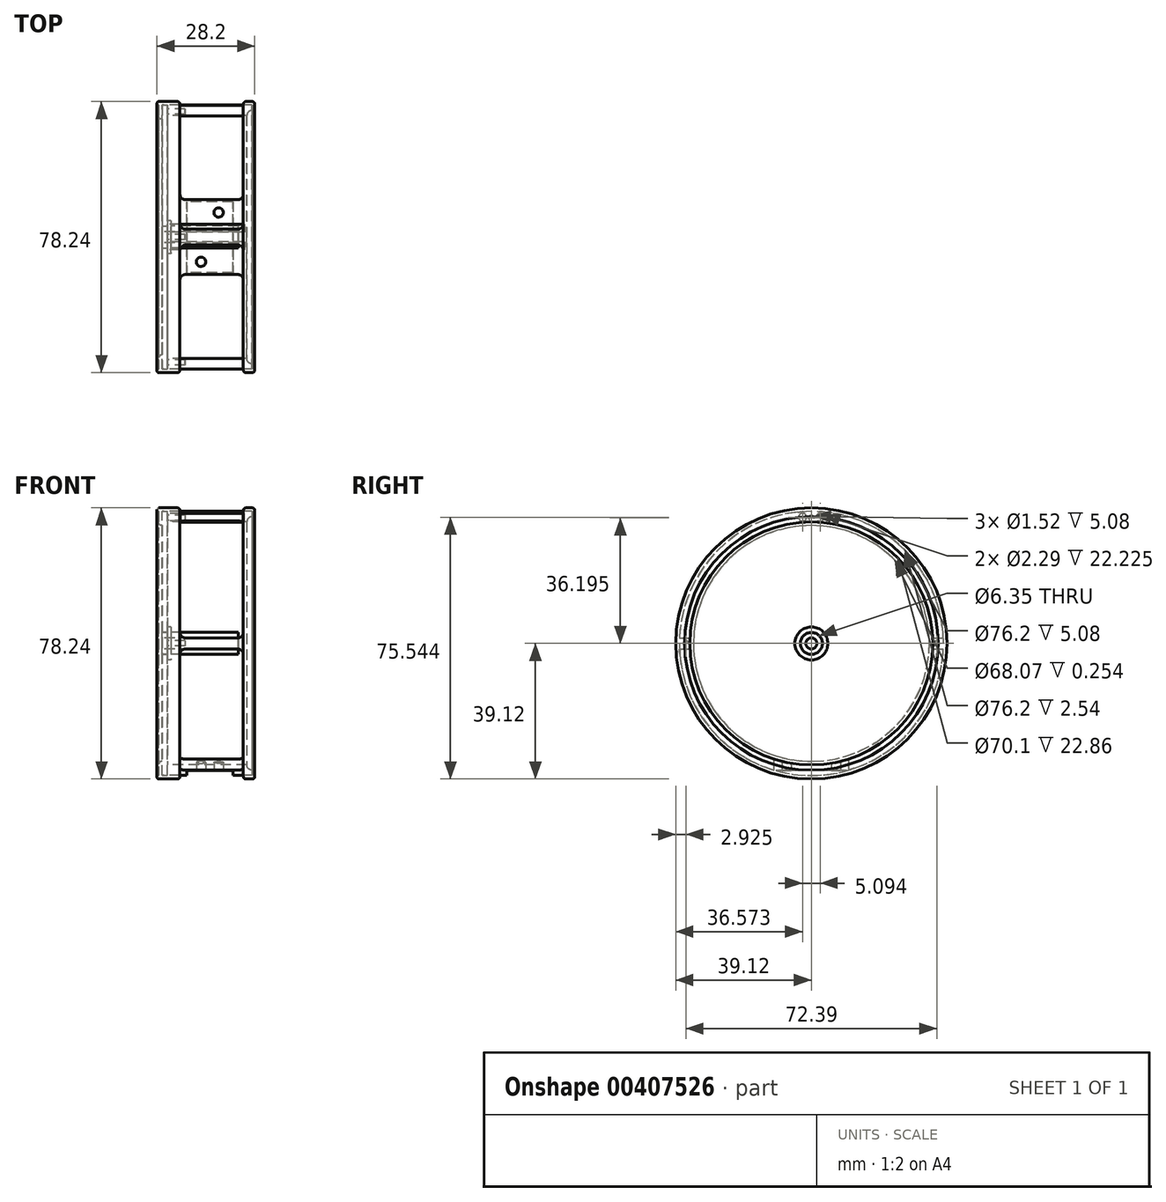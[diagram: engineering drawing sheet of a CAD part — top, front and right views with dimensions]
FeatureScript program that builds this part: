
annotation { "Feature Type Name" : "Feature", "Feature Type Description" : "" }
export const myFeature = defineFeature(function(context is Context, id is Id, definition is map)
    precondition{}
    {
        {
            var Q0;
            Q0=qCreatedBy(makeId("Front.planeOp"),FACE);
            var sketch = newSketch(context, id + "F0", { "sketchPlane" : qUnion([Q0])});
            skLineSegment(sketch, "E0", {"start": v(0, 38.1) * mm, "end": v(24.38, 38.1) * mm});
            skLineSegment(sketch, "E1", {"start": v(24.38, 38.1) * mm, "end": v(24.38, 36.58) * mm});
            skLineSegment(sketch, "E2", {"start": v(22.86, 35.05) * mm, "end": v(0, 35.05) * mm});
            skLineSegment(sketch, "E3", {"start": v(0, 0) * mm, "end": v(54.8, 0) * mm, "construction": true});
            skArc(sketch, "E4", {"start": v(22.86, 35.05) * mm, "mid": v(23.3, 36.13) * mm, "end": v(24.38, 36.58) * mm});
            skLineSegment(sketch, "E5", {"start": v(0, 38.1) * mm, "end": v(0, 35.05) * mm});
            skSolve(sketch);
        }
        {
            var Q0;
            Q0 = qSketchRegion(id + "F0", true);
            var Q1;
            Q1=sQuery(id+"F0.wireOp",EDGE,"E3");
            revolve(context, id + "F1", {"entities" : qUnion([Q0]), "axis" : qUnion([Q1]), "revolveType" : RevolveType.FULL});
        }
        {
            var Q0;
            Q0=makeQuery(id+"F1.opRevolve","SWEPT_FACE",FACE,{"disambiguationData":[OSD([sQuery(id+"F0.wireOp",EDGE,"E5")])]});
            var sketch = newSketch(context, id + "F2", { "sketchPlane" : qUnion([Q0])});
            skCircle(sketch, "E6", {"center": v(0, 0) * mm, "radius": 36.2 * mm, "construction": true});
            skCircle(sketch, "E7", {"center": v(0, 36.2) * mm, "radius": 0.76 * mm});
            skCircle(sketch, "E8", {"center": v(-36.2, 0) * mm, "radius": 0.76 * mm});
            skCircle(sketch, "E9", {"center": v(36.2, 0) * mm, "radius": 0.76 * mm});
            skSolve(sketch);
        }
        {
            var Q0;
            Q0 = qSketchRegion(id + "F2", true);
            extrude(context, id + "F3", {"entities" : qUnion([Q0]), "operationType" : NewBodyOperationType.REMOVE, "oppositeDirection" : true, "depth" : 5.08 * mm});
        }
        {
            var Q0;
            Q0=qCreatedBy(makeId("Right.planeOp"),FACE);
            var sketch = newSketch(context, id + "F4", { "sketchPlane" : qUnion([Q0])});
            skCircle(sketch, "E10", {"center": v(0, 0) * mm, "radius": 36.51 * mm, "construction": true});
            skLineSegment(sketch, "E11", {"start": v(2.55, 36.42) * mm, "end": v(0, 0) * mm, "construction": true});
            skCircle(sketch, "E12", {"center": v(2.55, 36.42) * mm, "radius": 1.14 * mm});
            skCircle(sketch, "E13.MirrorC", {"center": v(-2.55, 36.42) * mm, "radius": 1.14 * mm});
            skSolve(sketch);
        }
        {
            var Q0;
            Q0 = qSketchRegion(id + "F4", true);
            extrude(context, id + "F5", {"entities" : qUnion([Q0]), "operationType" : NewBodyOperationType.REMOVE, "depth" : 22.22 * mm, "offsetDistance" : 25.4 * mm});
        }
        {
            var Q0;
            Q0=qCreatedBy(makeId("Top.planeOp"),FACE);
            var sketch = newSketch(context, id + "F6", { "sketchPlane" : qUnion([Q0])});
            skCircle(sketch, "E14", {"center": v(5.14, 3.87) * mm, "radius": 1.59 * mm});
            skCircle(sketch, "E15", {"center": v(20.26, 3.87) * mm, "radius": 1.59 * mm});
            skLineSegment(sketch, "E16", {"start": v(5.14, 2.29) * mm, "end": v(20.26, 2.29) * mm});
            skCircle(sketch, "E17", {"center": v(5.14, 31.81) * mm, "radius": 1.59 * mm});
            skCircle(sketch, "E18", {"center": v(20.26, 31.81) * mm, "radius": 1.59 * mm});
            skLineSegment(sketch, "E19", {"start": v(3.56, 3.87) * mm, "end": v(3.56, 31.81) * mm});
            skLineSegment(sketch, "E20", {"start": v(21.84, 3.87) * mm, "end": v(21.84, 31.81) * mm});
            skLineSegment(sketch, "E21", {"start": v(5.14, 33.4) * mm, "end": v(20.26, 33.4) * mm});
            skCircle(sketch, "E22.MirrorC", {"center": v(20.26, -31.81) * mm, "radius": 1.59 * mm});
            skLineSegment(sketch, "E23.MirrorCS", {"start": v(21.84, -3.87) * mm, "end": v(21.84, -31.81) * mm});
            skLineSegment(sketch, "E24.MirrorCS", {"start": v(5.14, -33.4) * mm, "end": v(20.26, -33.4) * mm});
            skLineSegment(sketch, "E25.MirrorCS", {"start": v(3.56, -3.87) * mm, "end": v(3.56, -31.81) * mm});
            skCircle(sketch, "E26.MirrorC", {"center": v(5.14, -31.81) * mm, "radius": 1.59 * mm});
            skCircle(sketch, "E27.MirrorC", {"center": v(5.14, -3.87) * mm, "radius": 1.59 * mm});
            skCircle(sketch, "E28.MirrorC", {"center": v(20.26, -3.87) * mm, "radius": 1.59 * mm});
            skLineSegment(sketch, "E29.MirrorCS", {"start": v(5.14, -2.29) * mm, "end": v(20.26, -2.29) * mm});
            skSolve(sketch);
        }
        {
            var Q0;
            Q0 = qSketchRegion(id + "F6", true);
            extrude(context, id + "F7", {"entities" : qUnion([Q0]), "operationType" : NewBodyOperationType.REMOVE, "depth" : 304.8 * mm});
        }
        {
            var Q0;
            Q0=qCreatedBy(makeId("Front.planeOp"),FACE);
            var sketch = newSketch(context, id + "F8", { "sketchPlane" : qUnion([Q0])});
            skCircle(sketch, "E30", {"center": v(5.14, 3.17) * mm, "radius": 1.59 * mm});
            skCircle(sketch, "E31", {"center": v(20.26, 3.18) * mm, "radius": 1.59 * mm});
            skLineSegment(sketch, "E32", {"start": v(3.56, 3.17) * mm, "end": v(3.56, 33.02) * mm});
            skLineSegment(sketch, "E33", {"start": v(21.84, 3.18) * mm, "end": v(21.84, 33.02) * mm});
            skLineSegment(sketch, "E34", {"start": v(21.84, 33.02) * mm, "end": v(3.56, 33.02) * mm});
            skLineSegment(sketch, "E35", {"start": v(5.14, 1.59) * mm, "end": v(20.26, 1.59) * mm});
            skLineSegment(sketch, "E36.MirrorCS", {"start": v(21.84, -33.02) * mm, "end": v(3.56, -33.02) * mm});
            skLineSegment(sketch, "E37.MirrorCS", {"start": v(3.56, -3.17) * mm, "end": v(3.56, -33.02) * mm});
            skLineSegment(sketch, "E38.MirrorCS", {"start": v(21.84, -3.18) * mm, "end": v(21.84, -33.02) * mm});
            skCircle(sketch, "E39.MirrorC", {"center": v(20.26, -3.18) * mm, "radius": 1.59 * mm});
            skLineSegment(sketch, "E40.MirrorCS", {"start": v(5.14, -1.59) * mm, "end": v(20.26, -1.59) * mm});
            skCircle(sketch, "E41.MirrorC", {"center": v(5.14, -3.17) * mm, "radius": 1.59 * mm});
            skSolve(sketch);
        }
        {
            var Q0;
            Q0 = qSketchRegion(id + "F8", true);
            extrude(context, id + "F9", {"entities" : qUnion([Q0]), "operationType" : NewBodyOperationType.REMOVE, "endBound" : BoundingType.SYMMETRIC, "depth" : 88.9 * mm});
        }
        {
            var Q0;
            Q0=qCreatedBy(makeId("Top.planeOp"),FACE);
            var sketch = newSketch(context, id + "F10", { "sketchPlane" : qUnion([Q0])});
            skCircle(sketch, "E42", {"center": v(5.14, 12.38) * mm, "radius": 1.59 * mm});
            skCircle(sketch, "E43", {"center": v(20.26, 12.38) * mm, "radius": 1.59 * mm});
            skLineSegment(sketch, "E44", {"start": v(3.56, 12.38) * mm, "end": v(3.56, 33.4) * mm});
            skLineSegment(sketch, "E45", {"start": v(21.84, 12.38) * mm, "end": v(21.84, 33.4) * mm});
            skLineSegment(sketch, "E46", {"start": v(3.56, 33.4) * mm, "end": v(21.84, 33.4) * mm});
            skLineSegment(sketch, "E47", {"start": v(5.14, 10.8) * mm, "end": v(20.26, 10.8) * mm});
            skLineSegment(sketch, "E48.MirrorCS", {"start": v(5.14, -10.8) * mm, "end": v(20.26, -10.8) * mm});
            skCircle(sketch, "E49.MirrorC", {"center": v(5.14, -12.38) * mm, "radius": 1.59 * mm});
            skCircle(sketch, "E50.MirrorC", {"center": v(20.26, -12.38) * mm, "radius": 1.59 * mm});
            skLineSegment(sketch, "E51.MirrorCS", {"start": v(21.84, -12.38) * mm, "end": v(21.84, -33.4) * mm});
            skLineSegment(sketch, "E52.MirrorCS", {"start": v(3.56, -33.4) * mm, "end": v(21.84, -33.4) * mm});
            skLineSegment(sketch, "E53.MirrorCS", {"start": v(3.56, -12.38) * mm, "end": v(3.56, -33.4) * mm});
            skSolve(sketch);
        }
        {
            var Q0;
            Q0 = qSketchRegion(id + "F10", true);
            extrude(context, id + "F11", {"entities" : qUnion([Q0]), "operationType" : NewBodyOperationType.REMOVE, "oppositeDirection" : true, "depth" : 50.8 * mm});
        }
        {
            var Q0;
            Q0=qCreatedBy(makeId("Front.planeOp"),FACE);
            var sketch = newSketch(context, id + "F12", { "sketchPlane" : qUnion([Q0])});
            skLineSegment(sketch, "E54.bottom", {"start": v(18.86, -39.24) * mm, "end": v(5.52, -39.24) * mm});
            skLineSegment(sketch, "E54.top", {"start": v(18.86, -36.7) * mm, "end": v(5.52, -36.7) * mm});
            skLineSegment(sketch, "E54.left", {"start": v(18.86, -39.24) * mm, "end": v(18.86, -36.7) * mm});
            skLineSegment(sketch, "E54.right", {"start": v(5.52, -39.24) * mm, "end": v(5.52, -36.7) * mm});
            skPoint(sketch, "E54.middle", {"position": v(12.2, -37.97) * mm});
            skSolve(sketch);
        }
        {
            var Q0;
            Q0 = qSketchRegion(id + "F12", true);
            extrude(context, id + "F13", {"entities" : qUnion([Q0]), "operationType" : NewBodyOperationType.REMOVE, "endBound" : BoundingType.SYMMETRIC, "oppositeDirection" : true, "depth" : 25.4 * mm, "offsetDistance" : 25.4 * mm});
        }
        {
            var Q0;
            Q0=qCreatedBy(makeId("Front.planeOp"),FACE);
            var sketch = newSketch(context, id + "F14", { "sketchPlane" : qUnion([Q0])});
            skLineSegment(sketch, "E55", {"start": v(24.38, 36.58) * mm, "end": v(24.38, 38.1) * mm});
            skLineSegment(sketch, "E56", {"start": v(24.38, 38.1) * mm, "end": v(21.84, 38.1) * mm});
            skLineSegment(sketch, "E57", {"start": v(21.84, 38.1) * mm, "end": v(21.84, 39.12) * mm});
            skLineSegment(sketch, "E58", {"start": v(21.84, 39.12) * mm, "end": v(25.15, 39.12) * mm});
            skLineSegment(sketch, "E59", {"start": v(25.15, 39.12) * mm, "end": v(25.15, 36.58) * mm});
            skLineSegment(sketch, "E60", {"start": v(24.38, 36.58) * mm, "end": v(25.15, 36.58) * mm});
            skSolve(sketch);
        }
        {
            var Q0;
            Q0 = qSketchRegion(id + "F14", true);
            var Q1;
            Q1=sQuery(id+"F0.wireOp",EDGE,"E3");
            revolve(context, id + "F15", {"entities" : qUnion([Q0]), "axis" : qUnion([Q1]), "revolveType" : RevolveType.FULL});
        }
        {
            var Q0;
            Q0=makeQuery(id+"F15.opRevolve","SWEPT_EDGE",EDGE,{"disambiguationData":[OSD([sQuery(id+"F14.wireOp",EDGE,"E59"),sQuery(id+"F14.wireOp",EDGE,"E60")])]});
            var Q1;
            Q1=makeQuery(id+"F15.opRevolve","SWEPT_EDGE",EDGE,{"disambiguationData":[OSD([sQuery(id+"F14.wireOp",EDGE,"E58"),sQuery(id+"F14.wireOp",EDGE,"E59")])]});
            var Q2;
            Q2=makeQuery(id+"F15.opRevolve","SWEPT_EDGE",EDGE,{"disambiguationData":[OSD([sQuery(id+"F14.wireOp",EDGE,"E57"),sQuery(id+"F14.wireOp",EDGE,"E58")])]});
            fillet(context, id + "F16", {"entities" : qUnion([Q0, Q1, Q2]), "radius" : 0.76 * mm, "tangentPropagation" : true, "allowEdgeOverflow" : false});
        }
        {
            var Q0;
            Q0=qCreatedBy(makeId("Right.planeOp"),FACE);
            var sketch = newSketch(context, id + "F17", { "sketchPlane" : qUnion([Q0])});
            skCircle(sketch, "E61", {"center": v(0, 0) * mm, "radius": 38.1 * mm});
            skCircle(sketch, "E62", {"center": v(0, 0) * mm, "radius": 3.18 * mm});
            skSolve(sketch);
        }
        {
            var Q0;
            Q0 = qSketchRegion(id + "F17", true);
            extrude(context, id + "F18", {"entities" : qUnion([Q0]), "oppositeDirection" : true, "depth" : 1.52 * mm});
        }
        {
            var Q0;
            Q0=qCreatedBy(makeId("Front.planeOp"),FACE);
            var sketch = newSketch(context, id + "F19", { "sketchPlane" : qUnion([Q0])});
            skLineSegment(sketch, "E63", {"start": v(-1.52, 1.59) * mm, "end": v(-1.52, 3.18) * mm});
            skLineSegment(sketch, "E64", {"start": v(-1.52, 3.18) * mm, "end": v(0, 3.18) * mm});
            skLineSegment(sketch, "E65", {"start": v(0, 3.18) * mm, "end": v(0, 4.76) * mm});
            skLineSegment(sketch, "E66", {"start": v(0, 4.76) * mm, "end": v(1.02, 4.76) * mm});
            skLineSegment(sketch, "E67", {"start": v(1.02, 4.76) * mm, "end": v(1.02, 3.18) * mm});
            skLineSegment(sketch, "E68", {"start": v(1.02, 3.18) * mm, "end": v(20.45, 3.18) * mm});
            skLineSegment(sketch, "E69", {"start": v(20.45, 3.18) * mm, "end": v(20.45, 1.59) * mm});
            skLineSegment(sketch, "E70", {"start": v(20.45, 1.59) * mm, "end": v(-1.52, 1.59) * mm});
            skSolve(sketch);
        }
        {
            var Q0;
            Q0 = qSketchRegion(id + "F19", true);
            var Q1;
            Q1=sQuery(id+"F0.wireOp",EDGE,"E3");
            revolve(context, id + "F20", {"entities" : qUnion([Q0]), "axis" : qUnion([Q1]), "revolveType" : RevolveType.FULL});
        }
        {
            var Q0;
            Q0=qCreatedBy(makeId("Front.planeOp"),FACE);
            var sketch = newSketch(context, id + "F21", { "sketchPlane" : qUnion([Q0])});
            skLineSegment(sketch, "E71", {"start": v(3.56, 38.1) * mm, "end": v(-1.52, 38.1) * mm});
            skLineSegment(sketch, "E72", {"start": v(3.56, 38.1) * mm, "end": v(3.56, 39.12) * mm});
            skLineSegment(sketch, "E73", {"start": v(-1.52, 38.1) * mm, "end": v(-1.52, 34.04) * mm});
            skLineSegment(sketch, "E74", {"start": v(-1.52, 34.04) * mm, "end": v(-2.54, 34.04) * mm});
            skLineSegment(sketch, "E75", {"start": v(-2.54, 39.12) * mm, "end": v(3.56, 39.12) * mm});
            skArc(sketch, "E76", {"start": v(-2.54, 39.12) * mm, "mid": v(-3.05, 38.6) * mm, "end": v(-2.54, 38.1) * mm});
            skLineSegment(sketch, "E77", {"start": v(-2.54, 38.1) * mm, "end": v(-2.54, 34.04) * mm});
            skSolve(sketch);
        }
        {
            var Q0;
            Q0 = qSketchRegion(id + "F21", true);
            var Q1;
            Q1=sQuery(id+"F0.wireOp",EDGE,"E3");
            revolve(context, id + "F22", {"entities" : qUnion([Q0]), "axis" : qUnion([Q1]), "revolveType" : RevolveType.FULL});
        }
        {
            var Q0;
            Q0=makeQuery(id+"F22.opRevolve","SWEPT_EDGE",EDGE,{"disambiguationData":[OSD([sQuery(id+"F21.wireOp",EDGE,"E72"),sQuery(id+"F21.wireOp",EDGE,"E75")])]});
            var Q1;
            Q1=makeQuery(id+"F22.opRevolve","SWEPT_EDGE",EDGE,{"disambiguationData":[OSD([sQuery(id+"F21.wireOp",EDGE,"E74"),sQuery(id+"F21.wireOp",EDGE,"E77")])]});
            fillet(context, id + "F23", {"entities" : qUnion([Q0, Q1]), "radius" : 0.76 * mm, "tangentPropagation" : true, "allowEdgeOverflow" : false});
        }
        {
            var Q0;
            Q0=makeQuery(id+"F1.opRevolve","SWEPT_FACE",FACE,{"disambiguationData":[OSD([sQuery(id+"F0.wireOp",EDGE,"E5")])]});
            var sketch = newSketch(context, id + "F24", { "sketchPlane" : qUnion([Q0])});
            skCircle(sketch, "E78", {"center": v(-2.55, 36.42) * mm, "radius": 1.12 * mm});
            skSolve(sketch);
        }
        {
            var Q0;
            Q0 = qSketchRegion(id + "F24", true);
            extrude(context, id + "F25", {"entities" : qUnion([Q0]), "oppositeDirection" : true, "depth" : 22.1 * mm, "offsetDistance" : 25.4 * mm});
        }
        {
            var Q0;
            Q0=makeQuery(id+"F13.boolean.opBoolean","COPY",FACE,{"derivedFrom":makeQuery(id+"F13.opExtrude","SWEPT_FACE",FACE,{"disambiguationData":[OSD([sQuery(id+"F12.wireOp",EDGE,"E54.top")])]})});
            var sketch = newSketch(context, id + "F26", { "sketchPlane" : qUnion([Q0])});
            skLineSegment(sketch, "E79", {"start": v(18.86, 10.22) * mm, "end": v(5.52, -10.22) * mm, "construction": true});
            skPoint(sketch, "E80", {"position": v(12.2, 0) * mm});
            skPoint(sketch, "E81", {"position": v(9.65, 7.11) * mm});
            skPoint(sketch, "E82", {"position": v(14.73, -7.11) * mm});
            skSolve(sketch);
        }
        {
            var Q0;
            Q0=sQuery(id+"F26.wireOp",VERTEX,"E81");
            var Q1;
            Q1=sQuery(id+"F26.wireOp",VERTEX,"E82");
            var Q2;
            Q2=makeQuery(id+"F1.opRevolve","SWEPT_BODY",BODY,{"disambiguationData":[OSD([sQuery(id+"F0.wireOp",EDGE,"E0"),sQuery(id+"F0.wireOp",EDGE,"E1"),sQuery(id+"F0.wireOp",EDGE,"E2"),sQuery(id+"F0.wireOp",EDGE,"E4"),sQuery(id+"F0.wireOp",EDGE,"E5")])]});
            hole(context, id + "F27", {"style" : HoleStyle.SIMPLE, "endStyle" : HoleEndStyle.THROUGH, "standardTappedOrClearance" : lookupTablePath({ "standard" : "ANSI", "engagement" : "75%", "pitch" : "32 tpi", "size" : "#6", "type" : "Tapped" }), "standardBlindInLast" : lookupTablePath({ "standard" : "ANSI", "engagement" : "75%", "pitch" : "32 tpi", "size" : "#6", "type" : "Tapped" }), "holeDiameter" : 2.7 * mm, "majorDiameter" : 3.5 * mm, "showTappedDepth" : true, "tappedDepth" : 9.27 * mm, "tapClearance" : 3, "locations" : qUnion([Q0, Q1]), "scope" : qUnion([Q2])});
        }
    });
